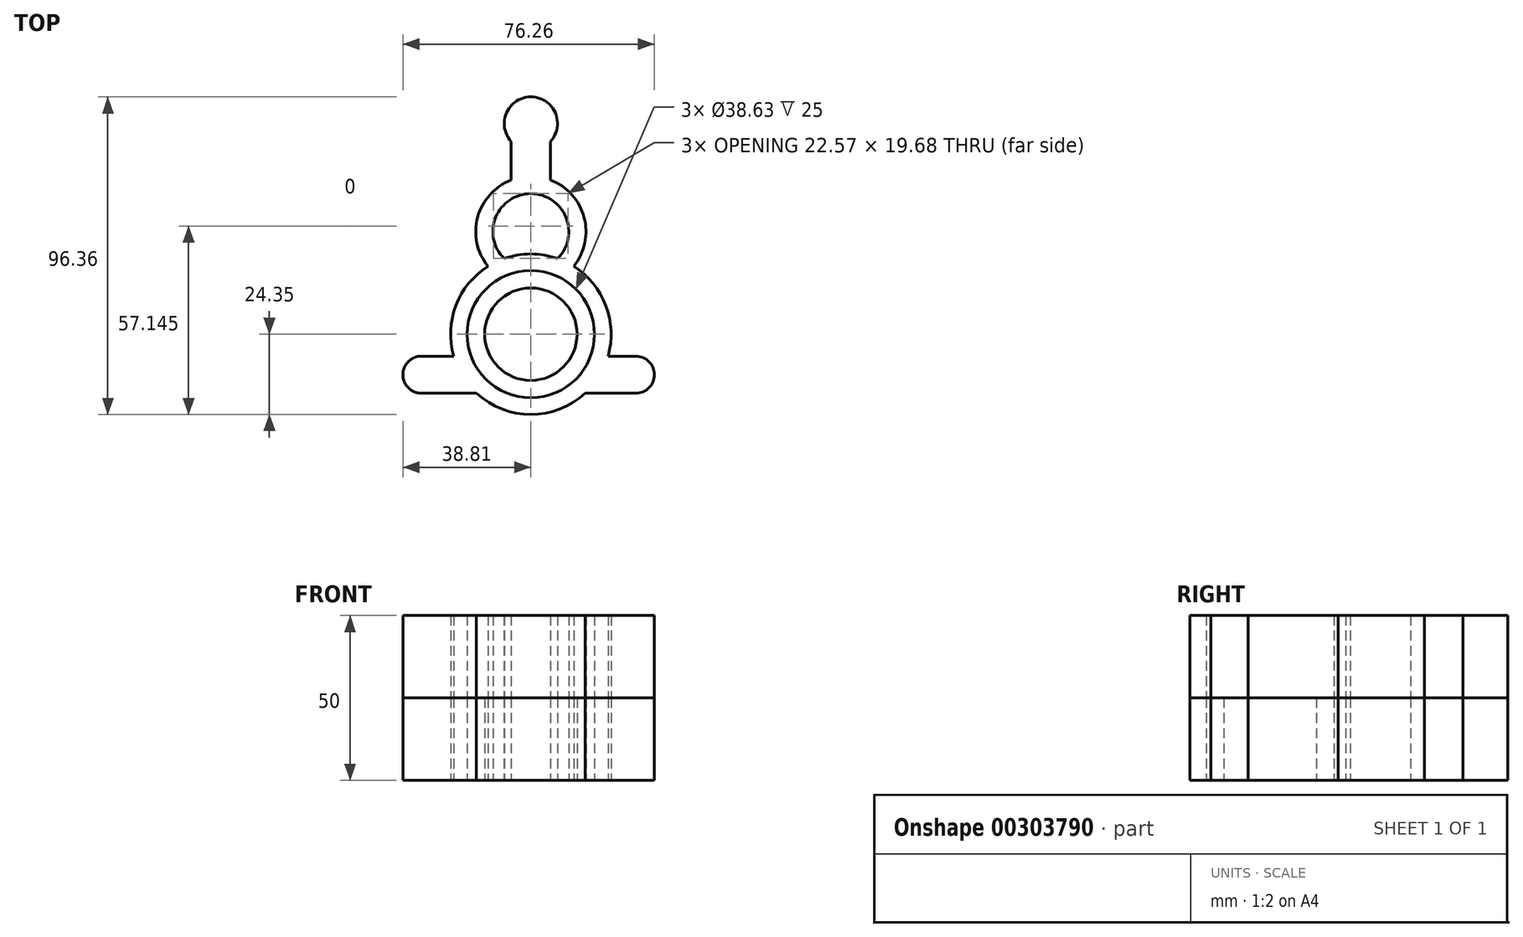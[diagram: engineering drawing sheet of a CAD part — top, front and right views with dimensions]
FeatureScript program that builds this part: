
annotation { "Feature Type Name" : "Feature", "Feature Type Description" : "" }
export const myFeature = defineFeature(function(context is Context, id is Id, definition is map)
    precondition{}
    {
        {
            var Q0;
            Q0=qCreatedBy(makeId("Top.planeOp"),FACE);
            var sketch = newSketch(context, id + "F0", { "sketchPlane" : qUnion([Q0])});
            skCircle(sketch, "E0", {"center": v(0, 0) * mm, "radius": 14.02 * mm});
            skCircle(sketch, "E1", {"center": v(0, 0) * mm, "radius": 19.31 * mm});
            skCircle(sketch, "E2", {"center": v(0, 0) * mm, "radius": 24.35 * mm});
            skCircle(sketch, "E3", {"center": v(-33.17, -12.3) * mm, "radius": 5.63 * mm});
            skCircle(sketch, "E4", {"center": v(31.83, -12.3) * mm, "radius": 5.63 * mm});
            skLineSegment(sketch, "E5", {"start": v(-33.17, -6.66) * mm, "end": v(-23.42, -6.67) * mm});
            skLineSegment(sketch, "E6", {"start": v(-33.17, -17.92) * mm, "end": v(-16.48, -17.92) * mm});
            skCircle(sketch, "E7", {"center": v(0, 31.12) * mm, "radius": 16.73 * mm});
            skArc(sketch, "E8", {"start": v(8.11, 22.96) * mm, "mid": v(0, 42.63) * mm, "end": v(-8.11, 22.96) * mm});
            skCircle(sketch, "E9", {"center": v(0, 63.95) * mm, "radius": 8.07 * mm});
            skLineSegment(sketch, "E10", {"start": v(-5.94, 46.76) * mm, "end": v(-5.94, 58.48) * mm});
            skLineSegment(sketch, "E11", {"start": v(5.94, 46.76) * mm, "end": v(5.94, 58.48) * mm});
            skLineSegment(sketch, "E12", {"start": v(31.83, -6.67) * mm, "end": v(23.42, -6.67) * mm});
            skLineSegment(sketch, "E13", {"start": v(31.83, -17.92) * mm, "end": v(16.48, -17.92) * mm});
            skSolve(sketch);
        }
        {
            var Q0;
            Q0 = qSketchRegion(id + "F0", true);
            extrude(context, id + "F1", {"entities" : qUnion([Q0]), "depth" : 25 * mm});
        }
        {
            var Q0;
            Q0=makeQuery(id+"F1.opExtrude","CAP_FACE",FACE,{"disambiguationData":[OSD([sQuery(id+"F0.wireOp",EDGE,"E4")])],"isStart":false});
            var sketch = newSketch(context, id + "F2", { "sketchPlane" : qUnion([Q0])});
            skSolve(sketch);
        }
        {
            var Q0;
            Q0 = qSketchRegion(id + "F0", true);
            var Q1;
            Q1=makeQuery(id+"F2.imprint","IMPRINT",FACE,{"disambiguationData":[TD([[makeQuery(id+"F2.imprint","IMPRINT",EDGE,{"derivedFrom":makeQuery(id+"F1.opExtrude","CAP_EDGE",EDGE,{"disambiguationData":[OSD([sQuery(id+"F0.wireOp",EDGE,"E4")])],"isStart":false})}),1.0]])]});
            var Q2;
            Q2=makeQuery(id+"F1.opExtrude","CAP_FACE",FACE,{"disambiguationData":[OSD([sQuery(id+"F0.wireOp",EDGE,"E1"),sQuery(id+"F0.wireOp",EDGE,"E2"),sQuery(id+"F0.wireOp",EDGE,"E3"),sQuery(id+"F0.wireOp",EDGE,"E5"),sQuery(id+"F0.wireOp",EDGE,"E6"),sQuery(id+"F0.wireOp",EDGE,"E7"),sQuery(id+"F0.wireOp",EDGE,"E8"),sQuery(id+"F0.wireOp",EDGE,"E9"),sQuery(id+"F0.wireOp",EDGE,"E10"),sQuery(id+"F0.wireOp",EDGE,"E11")])],"isStart":false});
            var Q3;
            Q3=makeQuery(id+"F0.imprint","IMPRINT",FACE,{"disambiguationData":[TD([[makeQuery(id+"F0.imprint","IMPRINT",EDGE,{"derivedFrom":sQuery(id+"F0.wireOp",EDGE,"E0")}),1.0]])]});
            var Q4;
            Q4=makeQuery(id+"F2.imprint","IMPRINT",FACE,{"disambiguationData":[TD([[makeQuery(id+"F2.imprint","IMPRINT",EDGE,{"derivedFrom":makeQuery(id+"F1.opExtrude","CAP_EDGE",EDGE,{"disambiguationData":[OSD([sQuery(id+"F0.wireOp",EDGE,"E1")])],"isStart":false})}),1.0]])]});
            var Q5;
            {var subQ0=sQuery(id+"F0.wireOp",EDGE,"E8");Q5=makeQuery(id+"F2.imprint","IMPRINT",FACE,{"disambiguationData":[TD([[makeQuery(id+"F2.imprint","IMPRINT",EDGE,{"derivedFrom":makeQuery(id+"F1.opExtrude","CAP_EDGE",EDGE,{"disambiguationData":[OSD([subQ0])],"isStart":false})}),1.0]])]});}
            extrude(context, id + "F3", {"entities" : qUnion([Q0, Q1, Q2, Q3, Q4, Q5]), "depth" : 25 * mm});
        }
    });
